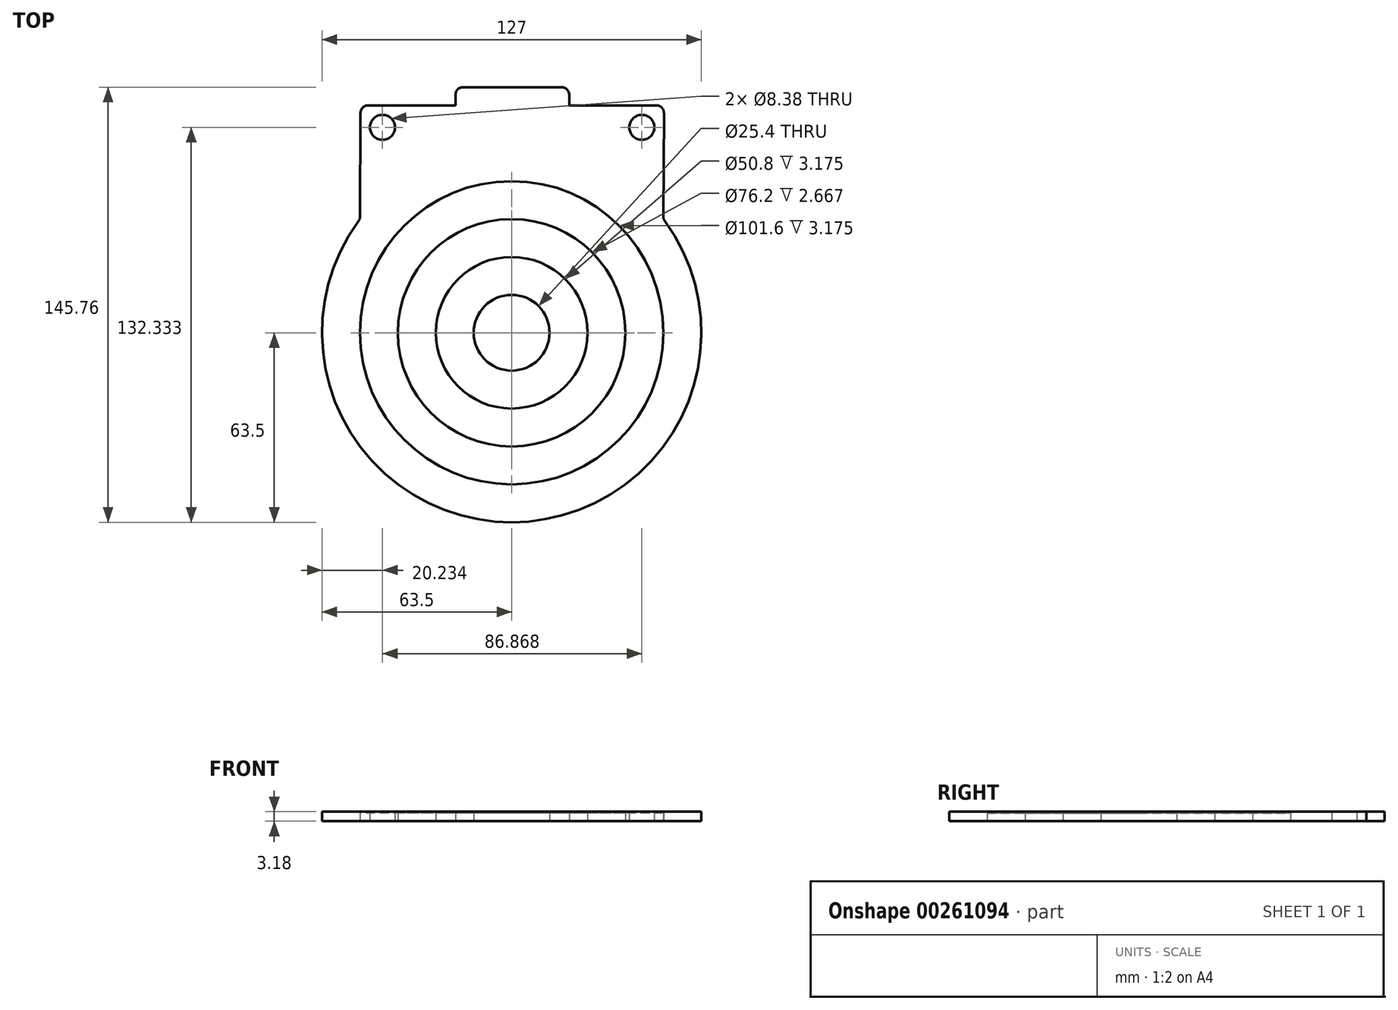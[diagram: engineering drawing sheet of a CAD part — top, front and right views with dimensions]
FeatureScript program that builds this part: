
annotation { "Feature Type Name" : "Feature", "Feature Type Description" : "" }
export const myFeature = defineFeature(function(context is Context, id is Id, definition is map)
    precondition{}
    {
        {
            var Q0;
            Q0=qCreatedBy(makeId("Top.planeOp"),FACE);
            var sketch = newSketch(context, id + "F0", { "sketchPlane" : qUnion([Q0])});
            skCircle(sketch, "E0", {"center": v(0, 0) * mm, "radius": 63.5 * mm, "construction": true});
            skLineSegment(sketch, "E1.left", {"start": v(-50.8, 38.1) * mm, "end": v(-50.6, 76.2) * mm});
            skLineSegment(sketch, "E1.right", {"start": v(50.8, 38.1) * mm, "end": v(51, 76.2) * mm});
            skLineSegment(sketch, "E2", {"start": v(0, 63.5) * mm, "end": v(0, 75.32) * mm, "construction": true});
            skArc(sketch, "E3", {"start": v(-50.8, 38.1) * mm, "mid": v(0, -63.5) * mm, "end": v(50.8, 38.1) * mm});
            skCircle(sketch, "E4", {"center": v(-43.27, 68.83) * mm, "radius": 4.2 * mm});
            skCircle(sketch, "E5", {"center": v(43.6, 68.83) * mm, "radius": 4.2 * mm});
            skLineSegment(sketch, "E6", {"start": v(-43.27, 68.83) * mm, "end": v(43.6, 68.83) * mm, "construction": true});
            skCircle(sketch, "E7", {"center": v(0, 0) * mm, "radius": 50.8 * mm});
            skCircle(sketch, "E8", {"center": v(0, 0) * mm, "radius": 38.1 * mm});
            skCircle(sketch, "E9", {"center": v(0, 0) * mm, "radius": 25.4 * mm});
            skCircle(sketch, "E10", {"center": v(0, 0) * mm, "radius": 12.7 * mm});
            skLineSegment(sketch, "E11.top", {"start": v(-18.84, 82.26) * mm, "end": v(19.26, 82.26) * mm});
            skLineSegment(sketch, "E11.left", {"start": v(-18.84, 76.2) * mm, "end": v(-18.84, 82.26) * mm});
            skLineSegment(sketch, "E11.right", {"start": v(19.26, 76.2) * mm, "end": v(19.26, 82.26) * mm});
            skLineSegment(sketch, "E12", {"start": v(-50.6, 76.2) * mm, "end": v(-18.84, 76.2) * mm});
            skLineSegment(sketch, "E13", {"start": v(19.26, 76.2) * mm, "end": v(51, 76.2) * mm});
            skSolve(sketch);
        }
        {
            var Q0;
            Q0=makeQuery(id+"F0.imprint","IMPRINT",FACE,{"disambiguationData":[TD([[makeQuery(id+"F0.imprint","IMPRINT",EDGE,{"derivedFrom":sQuery(id+"F0.wireOp",EDGE,"E8")}),1.0]])]});
            var Q1;
            Q1=makeQuery(id+"F0.imprint","IMPRINT",FACE,{"disambiguationData":[TD([[makeQuery(id+"F0.imprint","IMPRINT",EDGE,{"derivedFrom":sQuery(id+"F0.wireOp",EDGE,"E10")}),1.0]])]});
            var Q2;
            Q2=makeQuery(id+"F0.imprint","IMPRINT",FACE,{"disambiguationData":[TD([[makeQuery(id+"F0.imprint","IMPRINT",EDGE,{"derivedFrom":sQuery(id+"F0.wireOp",EDGE,"E1.top")}),-1.0]])]});
            var Q3;
            Q3=makeQuery(id+"F0.imprint","IMPRINT",FACE,{"disambiguationData":[TD([[makeQuery(id+"F0.imprint","IMPRINT",EDGE,{"derivedFrom":sQuery(id+"F0.wireOp",EDGE,"E1.left")}),-1.0]])]});
            extrude(context, id + "F1", {"entities" : qUnion([Q0, Q1, Q2, Q3]), "depth" : 3.17 * mm});
        }
        {
            var Q0;
            Q0=makeQuery(id+"F0.imprint","IMPRINT",FACE,{"disambiguationData":[TD([[makeQuery(id+"F0.imprint","IMPRINT",EDGE,{"derivedFrom":sQuery(id+"F0.wireOp",EDGE,"E7")}),1.0]])]});
            var Q1;
            Q1=makeQuery(id+"F0.imprint","IMPRINT",FACE,{"disambiguationData":[TD([[makeQuery(id+"F0.imprint","IMPRINT",EDGE,{"derivedFrom":sQuery(id+"F0.wireOp",EDGE,"E9")}),1.0]])]});
            extrude(context, id + "F2", {"entities" : qUnion([Q0, Q1]), "depth" : 2.67 * mm});
        }
        {
            var Q0;
            Q0=makeQuery(id+"F1.opExtrude","SWEPT_EDGE",EDGE,{"disambiguationData":[OSD([sQuery(id+"F0.wireOp",EDGE,"E11.top"),sQuery(id+"F0.wireOp",EDGE,"E11.left")])]});
            var Q1;
            Q1=makeQuery(id+"F1.opExtrude","SWEPT_EDGE",EDGE,{"disambiguationData":[OSD([sQuery(id+"F0.wireOp",EDGE,"E11.top"),sQuery(id+"F0.wireOp",EDGE,"E11.right")])]});
            var Q2;
            Q2=makeQuery(id+"F1.opExtrude","SWEPT_EDGE",EDGE,{"disambiguationData":[OSD([sQuery(id+"F0.wireOp",EDGE,"E1.left"),sQuery(id+"F0.wireOp",EDGE,"E12")])]});
            var Q3;
            Q3=makeQuery(id+"F1.opExtrude","SWEPT_EDGE",EDGE,{"disambiguationData":[OSD([sQuery(id+"F0.wireOp",EDGE,"E1.right"),sQuery(id+"F0.wireOp",EDGE,"E13")])]});
            var Q4;
            Q4=makeQuery(id+"F1.opExtrude","SWEPT_EDGE",EDGE,{"disambiguationData":[OSD([sQuery(id+"F0.wireOp",EDGE,"E1.left"),sQuery(id+"F0.wireOp",EDGE,"E3")])]});
            var Q5;
            Q5=makeQuery(id+"F1.opExtrude","SWEPT_EDGE",EDGE,{"disambiguationData":[OSD([sQuery(id+"F0.wireOp",EDGE,"E1.right"),sQuery(id+"F0.wireOp",EDGE,"E3")])]});
            fillet(context, id + "F3", {"entities" : qUnion([Q0, Q1, Q2, Q3, Q4, Q5]), "radius" : 2.54 * mm, "tangentPropagation" : true, "allowEdgeOverflow" : false});
        }
    });
